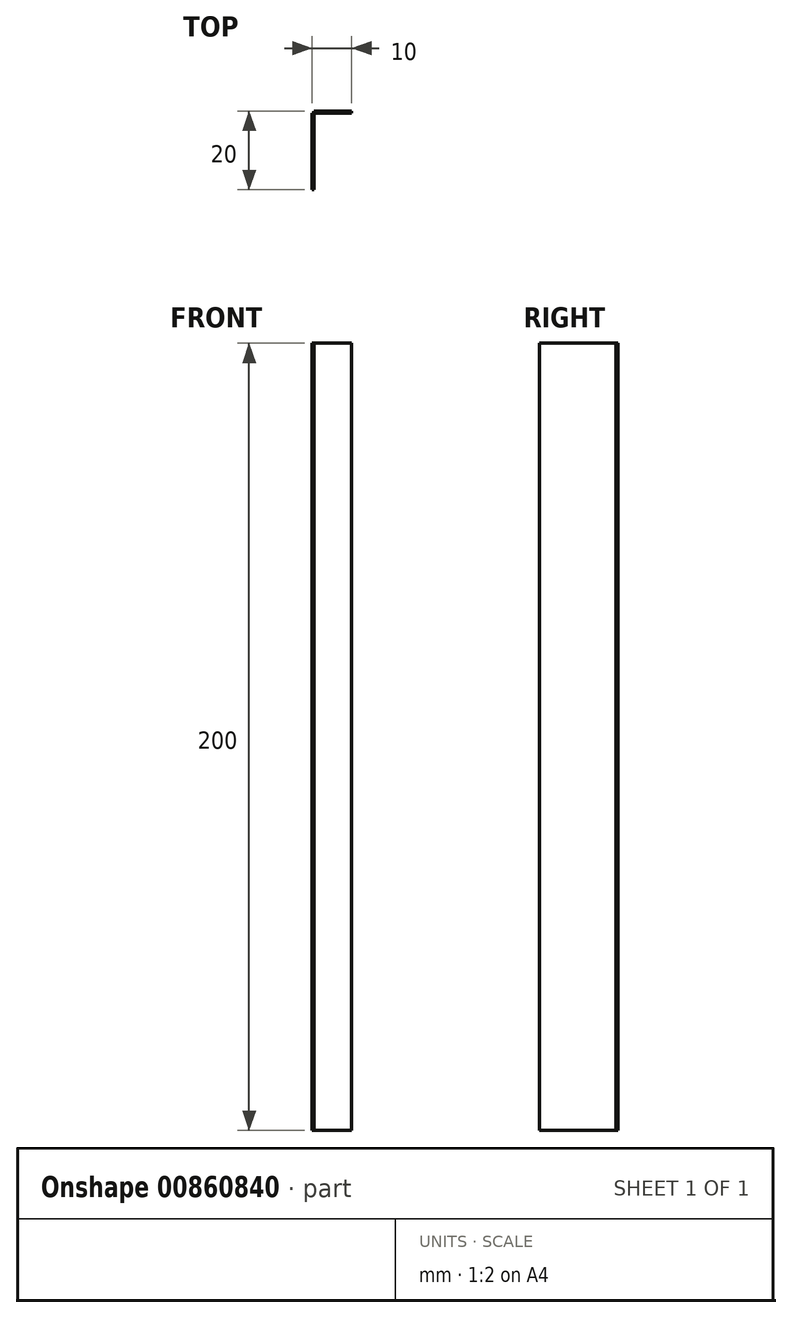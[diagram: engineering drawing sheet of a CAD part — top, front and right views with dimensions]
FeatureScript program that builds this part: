
annotation { "Feature Type Name" : "Feature", "Feature Type Description" : "" }
export const myFeature = defineFeature(function(context is Context, id is Id, definition is map)
    precondition{}
    {
        {
            var Q0;
            Q0=qCreatedBy(makeId("Top.planeOp"),FACE);
            var sketch = newSketch(context, id + "F0", { "sketchPlane" : qUnion([Q0])});
            skPoint(sketch, "E0.firstSnap0", {"position": v(-72.84, 7.8) * mm});
            skLineSegment(sketch, "E1.bottom", {"start": v(-78.03, 12.55) * mm, "end": v(-77.53, 12.55) * mm});
            skLineSegment(sketch, "E1.top", {"start": v(-78.03, -7.45) * mm, "end": v(-77.53, -7.45) * mm});
            skLineSegment(sketch, "E1.left", {"start": v(-78.03, 12.55) * mm, "end": v(-78.03, -7.45) * mm});
            skLineSegment(sketch, "E1.right", {"start": v(-77.53, 12.55) * mm, "end": v(-77.53, -7.45) * mm});
            skLineSegment(sketch, "E2.bottom", {"start": v(-78.03, 12.55) * mm, "end": v(-68.03, 12.55) * mm});
            skLineSegment(sketch, "E2.top", {"start": v(-78.03, 12.05) * mm, "end": v(-68.03, 12.05) * mm});
            skLineSegment(sketch, "E2.left", {"start": v(-78.03, 12.55) * mm, "end": v(-78.03, 12.05) * mm});
            skLineSegment(sketch, "E2.right", {"start": v(-68.03, 12.55) * mm, "end": v(-68.03, 12.05) * mm});
            skSolve(sketch);
        }
        {
            var Q0;
            {var subQ5=sQuery(id+"F0.wireOp",EDGE,"E2.right");Q0=makeQuery(id+"F0.imprint","IMPRINT",FACE,{"disambiguationData":[TD([[makeQuery(id+"F0.imprint","IMPRINT",EDGE,{"derivedFrom":subQ5}),-1.0]])]});}
            var Q1;
            {var subQ0=sQuery(id+"F0.wireOp",EDGE,"E1.top");Q1=makeQuery(id+"F0.imprint","IMPRINT",FACE,{"disambiguationData":[TD([[makeQuery(id+"F0.imprint","IMPRINT",EDGE,{"derivedFrom":subQ0}),1.0]])]});}
            var Q2;
            {var subQ5=sQuery(id+"F0.wireOp",EDGE,"E2.left");Q2=makeQuery(id+"F0.imprint","IMPRINT",FACE,{"disambiguationData":[TD([[makeQuery(id+"F0.imprint","IMPRINT",EDGE,{"derivedFrom":subQ5}),1.0]])]});}
            extrude(context, id + "F1", {"entities" : qUnion([Q0, Q1, Q2]), "depth" : 200 * mm, "offsetDistance" : 25 * mm});
        }
    });
